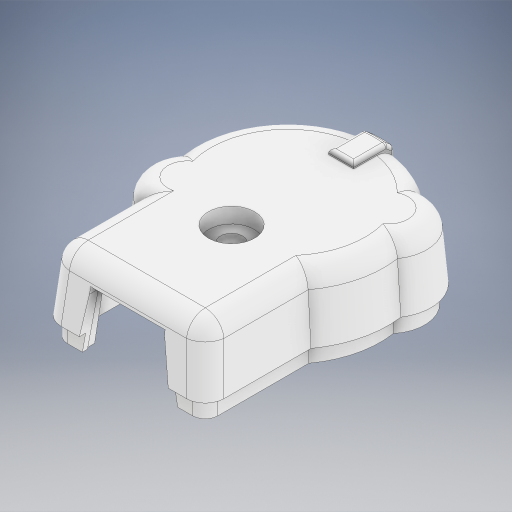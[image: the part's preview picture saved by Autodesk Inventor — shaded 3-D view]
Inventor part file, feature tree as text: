
AUTODESK INVENTOR PART (.ipt)
format: ipt  version: 2024.2 (Build 282272000, 272)  size: 568,832 bytes
history: native  units: in
note: dims shown in document units (in); Inventor stores cm internally (conversion verified against a paired STEP export)
features: fillet x1
ambient origin geometry x8: Origin, YZ Plane, XZ Plane, XY Plane, X Axis, Y Axis, Z Axis, Center Point
bodies: Solid1 (feature_tree)
feature tree (1):
  fillet  "Fillet18"  [1 undecoded]
note: 1 required parameter value undecoded (feature->parameter linkage not recoverable at this tier; creation-order binding heuristic only, values carry confidence <= 0.55)
